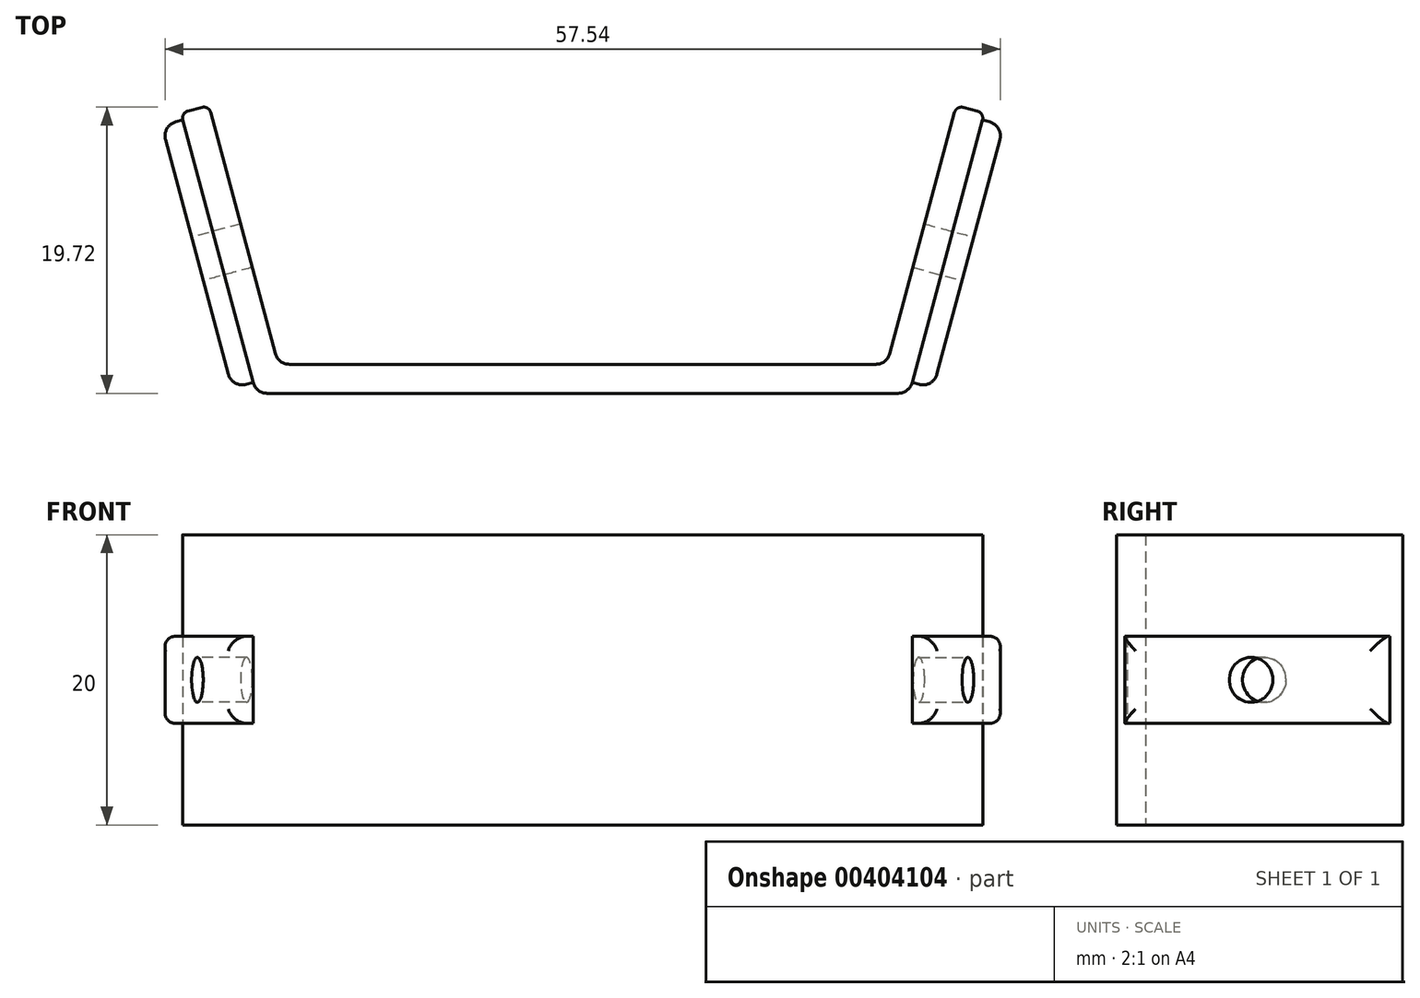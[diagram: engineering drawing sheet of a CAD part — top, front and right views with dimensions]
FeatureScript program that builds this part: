
annotation { "Feature Type Name" : "Feature", "Feature Type Description" : "" }
export const myFeature = defineFeature(function(context is Context, id is Id, definition is map)
    precondition{}
    {
        {
            var Q0;
            Q0=qCreatedBy(makeId("Top.planeOp"),FACE);
            var sketch = newSketch(context, id + "F0", { "sketchPlane" : qUnion([Q0])});
            skLineSegment(sketch, "E0", {"start": v(0.77, 0) * mm, "end": v(44.23, 0) * mm});
            skLineSegment(sketch, "E1", {"start": v(45.2, 0.74) * mm, "end": v(50.05, 18.84) * mm});
            skLineSegment(sketch, "E2", {"start": v(49.7, 19.45) * mm, "end": v(48.73, 19.7) * mm});
            skLineSegment(sketch, "E3", {"start": v(48.12, 19.35) * mm, "end": v(43.66, 2.74) * mm});
            skLineSegment(sketch, "E4", {"start": v(42.7, 2) * mm, "end": v(2.3, 2) * mm});
            skLineSegment(sketch, "E5", {"start": v(1.34, 2.74) * mm, "end": v(-3.12, 19.35) * mm});
            skLineSegment(sketch, "E6", {"start": v(-3.73, 19.7) * mm, "end": v(-4.7, 19.45) * mm});
            skLineSegment(sketch, "E7", {"start": v(-5.05, 18.84) * mm, "end": v(-0.2, 0.74) * mm});
            skPoint(sketch, "E8.visualSharp", {"position": v(-3.24, 19.84) * mm});
            skArc(sketch, "E8.filletArc", {"start": v(-3.12, 19.35) * mm, "mid": v(-3.35, 19.66) * mm, "end": v(-3.73, 19.7) * mm});
            skPoint(sketch, "E9.visualSharp", {"position": v(-5.18, 19.32) * mm});
            skArc(sketch, "E9.filletArc", {"start": v(-4.7, 19.45) * mm, "mid": v(-5, 19.21) * mm, "end": v(-5.05, 18.84) * mm});
            skPoint(sketch, "E10.visualSharp", {"position": v(0, 0) * mm});
            skArc(sketch, "E10.filletArc", {"start": v(-0.2, 0.74) * mm, "mid": v(0.16, 0.2) * mm, "end": v(0.77, 0) * mm});
            skPoint(sketch, "E11.visualSharp", {"position": v(1.53, 2) * mm});
            skArc(sketch, "E11.filletArc", {"start": v(1.34, 2.74) * mm, "mid": v(1.7, 2.2) * mm, "end": v(2.3, 2) * mm});
            skPoint(sketch, "E12.visualSharp", {"position": v(45, 0) * mm});
            skArc(sketch, "E12.filletArc", {"start": v(44.23, 0) * mm, "mid": v(44.84, 0.2) * mm, "end": v(45.2, 0.74) * mm});
            skPoint(sketch, "E13.visualSharp", {"position": v(43.47, 2) * mm});
            skArc(sketch, "E13.filletArc", {"start": v(42.7, 2) * mm, "mid": v(43.3, 2.2) * mm, "end": v(43.66, 2.74) * mm});
            skPoint(sketch, "E14.visualSharp", {"position": v(48.24, 19.84) * mm});
            skArc(sketch, "E14.filletArc", {"start": v(48.73, 19.7) * mm, "mid": v(48.35, 19.66) * mm, "end": v(48.12, 19.35) * mm});
            skPoint(sketch, "E15.visualSharp", {"position": v(50.18, 19.32) * mm});
            skArc(sketch, "E15.filletArc", {"start": v(50.05, 18.84) * mm, "mid": v(50, 19.21) * mm, "end": v(49.7, 19.45) * mm});
            skSolve(sketch);
        }
        {
            var Q0;
            Q0=qSketchRegion(id+"F0",true);
            extrude(context, id + "F1", {"entities" : qUnion([Q0]), "depth" : 20 * mm});
        }
        {
            var Q0;
            Q0=makeQuery(id+"F1.opExtrude","SWEPT_FACE",FACE,{"disambiguationData":[OSD([sQuery(id+"F0.wireOp",EDGE,"E1")])]});
            var sketch = newSketch(context, id + "F2", { "sketchPlane" : qUnion([Q0])});
            skLineSegment(sketch, "E16.bottom", {"start": v(31.15, 7) * mm, "end": v(12.41, 7) * mm});
            skLineSegment(sketch, "E16.top", {"start": v(31.15, 13) * mm, "end": v(12.41, 13) * mm});
            skLineSegment(sketch, "E16.left", {"start": v(31.15, 7) * mm, "end": v(31.15, 13) * mm});
            skLineSegment(sketch, "E16.right", {"start": v(12.41, 7) * mm, "end": v(12.41, 13) * mm});
            skSolve(sketch);
        }
        {
            var Q0;
            Q0=qSketchRegion(id+"F2",true);
            extrude(context, id + "F3", {"entities" : qUnion([Q0]), "operationType" : NewBodyOperationType.ADD, "depth" : 1.5 * mm});
        }
        {
            var Q0;
            Q0=makeQuery(id+"F1.opExtrude","SWEPT_FACE",FACE,{"disambiguationData":[OSD([sQuery(id+"F0.wireOp",EDGE,"E7")])]});
            var sketch = newSketch(context, id + "F4", { "sketchPlane" : qUnion([Q0])});
            skLineSegment(sketch, "E17.bottom", {"start": v(-0.77, 7) * mm, "end": v(-19.5, 7) * mm});
            skLineSegment(sketch, "E17.top", {"start": v(-0.77, 13) * mm, "end": v(-19.5, 13) * mm});
            skLineSegment(sketch, "E17.left", {"start": v(-0.77, 7) * mm, "end": v(-0.77, 13) * mm});
            skLineSegment(sketch, "E17.right", {"start": v(-19.5, 7) * mm, "end": v(-19.5, 13) * mm});
            skSolve(sketch);
        }
        {
            var Q0;
            Q0=qSketchRegion(id+"F4",true);
            extrude(context, id + "F5", {"entities" : qUnion([Q0]), "operationType" : NewBodyOperationType.ADD, "depth" : 1.5 * mm});
        }
        {
            var Q0;
            Q0=makeQuery(id+"F1.opExtrude","SWEPT_FACE",FACE,{"disambiguationData":[OSD([sQuery(id+"F0.wireOp",EDGE,"E7")])]});
            var sketch = newSketch(context, id + "F6", { "sketchPlane" : qUnion([Q0])});
            skCircle(sketch, "E18", {"center": v(-10, 10) * mm, "radius": 1.55 * mm});
            skSolve(sketch);
        }
        {
            var Q0;
            Q0=qSketchRegion(id+"F6",true);
            extrude(context, id + "F7", {"entities" : qUnion([Q0]), "operationType" : NewBodyOperationType.REMOVE, "endBound" : BoundingType.SYMMETRIC, "oppositeDirection" : true, "depth" : 25 * mm});
        }
        {
            var Q0;
            Q0=makeQuery(id+"F1.opExtrude","SWEPT_FACE",FACE,{"disambiguationData":[OSD([sQuery(id+"F0.wireOp",EDGE,"E1")])]});
            var sketch = newSketch(context, id + "F8", { "sketchPlane" : qUnion([Q0])});
            skCircle(sketch, "E19", {"center": v(21.65, 10) * mm, "radius": 1.55 * mm});
            skSolve(sketch);
        }
        {
            var Q0;
            Q0=qSketchRegion(id+"F8",true);
            extrude(context, id + "F9", {"entities" : qUnion([Q0]), "operationType" : NewBodyOperationType.REMOVE, "endBound" : BoundingType.SYMMETRIC, "oppositeDirection" : true, "depth" : 25 * mm});
        }
        {
            var Q0;
            Q0=makeQuery(id+"F5.opExtrude","CAP_EDGE",EDGE,{"disambiguationData":[OSD([sQuery(id+"F4.wireOp",EDGE,"E17.left")])],"isStart":false});
            var Q1;
            Q1=makeQuery(id+"F5.opExtrude","CAP_EDGE",EDGE,{"disambiguationData":[OSD([sQuery(id+"F4.wireOp",EDGE,"E17.bottom")])],"isStart":false});
            var Q2;
            Q2=makeQuery(id+"F5.opExtrude","CAP_EDGE",EDGE,{"disambiguationData":[OSD([sQuery(id+"F4.wireOp",EDGE,"E17.top")])],"isStart":false});
            var Q3;
            Q3=makeQuery(id+"F5.opExtrude","CAP_EDGE",EDGE,{"disambiguationData":[OSD([sQuery(id+"F4.wireOp",EDGE,"E17.right")])],"isStart":false});
            var Q4;
            Q4=makeQuery(id+"F3.opExtrude","CAP_EDGE",EDGE,{"disambiguationData":[OSD([sQuery(id+"F2.wireOp",EDGE,"E16.left")])],"isStart":false});
            var Q5;
            Q5=makeQuery(id+"F3.opExtrude","CAP_EDGE",EDGE,{"disambiguationData":[OSD([sQuery(id+"F2.wireOp",EDGE,"E16.bottom")])],"isStart":false});
            var Q6;
            Q6=makeQuery(id+"F3.opExtrude","CAP_EDGE",EDGE,{"disambiguationData":[OSD([sQuery(id+"F2.wireOp",EDGE,"E16.top")])],"isStart":false});
            var Q7;
            Q7=makeQuery(id+"F3.opExtrude","CAP_EDGE",EDGE,{"disambiguationData":[OSD([sQuery(id+"F2.wireOp",EDGE,"E16.right")])],"isStart":false});
            fillet(context, id + "F10", {"entities" : qUnion([Q0, Q1, Q2, Q3, Q4, Q5, Q6, Q7]), "radius" : 1 * mm, "tangentPropagation" : true, "allowEdgeOverflow" : false});
        }
    });
